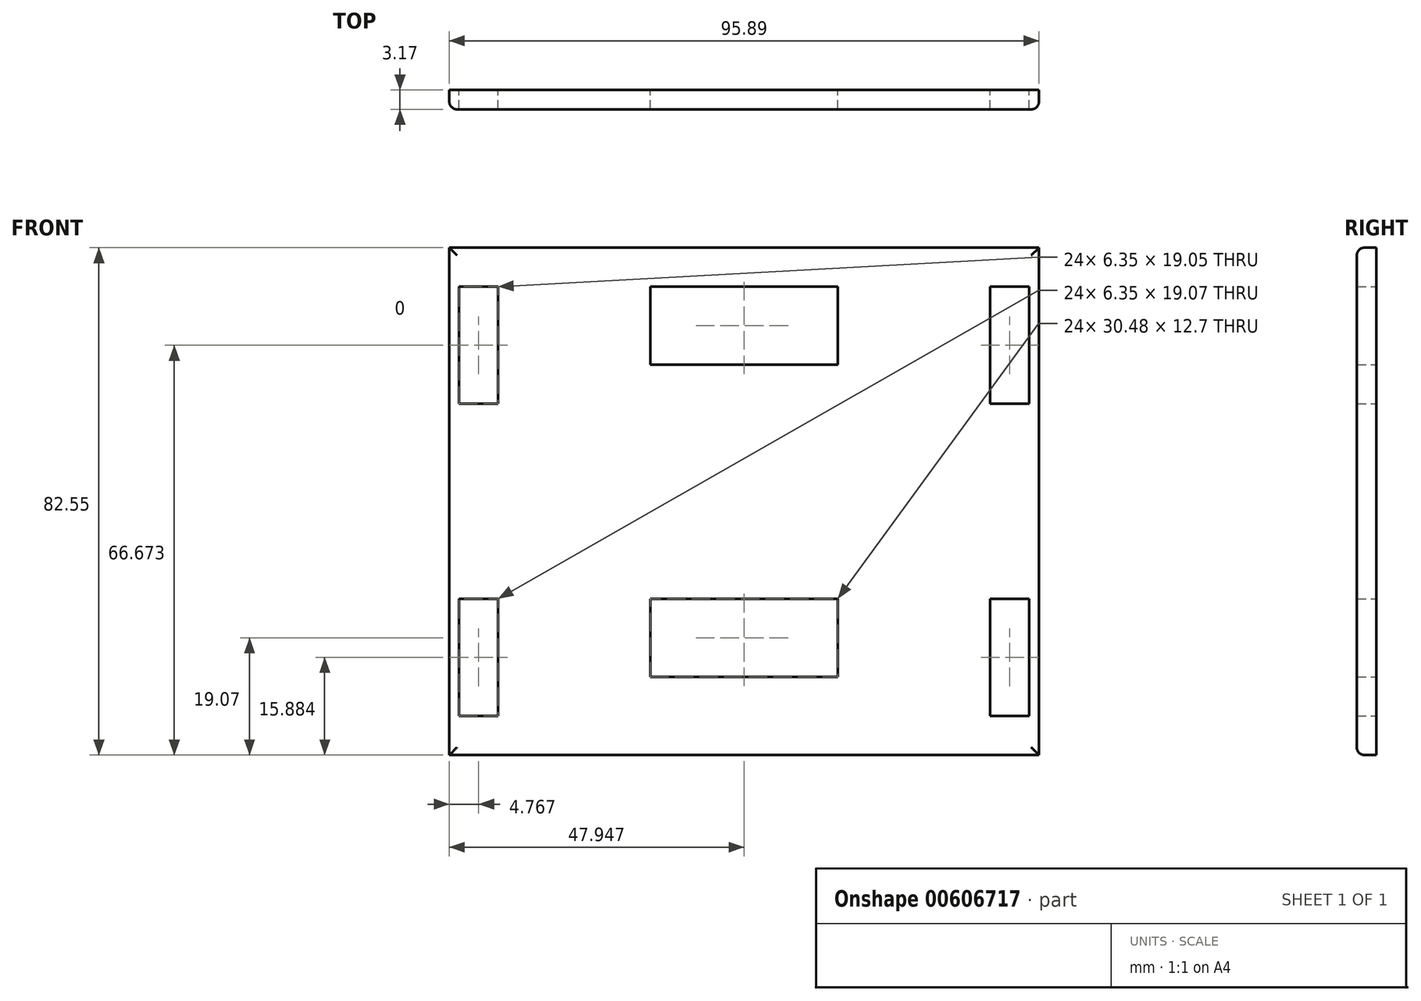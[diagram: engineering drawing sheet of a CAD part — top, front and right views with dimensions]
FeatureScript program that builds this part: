
annotation { "Feature Type Name" : "Feature", "Feature Type Description" : "" }
export const myFeature = defineFeature(function(context is Context, id is Id, definition is map)
    precondition{}
    {
        {
            var Q0;
            Q0=qCreatedBy(makeId("Front.planeOp"),FACE);
            var sketch = newSketch(context, id + "F0", { "sketchPlane" : qUnion([Q0])});
            skLineSegment(sketch, "E0", {"start": v(-18.63, 68.66) * mm, "end": v(-18.63, -13.9) * mm});
            skLineSegment(sketch, "E1", {"start": v(-13.86, 62.3) * mm, "end": v(-10.69, 62.3) * mm});
            skLineSegment(sketch, "E2", {"start": v(-10.69, 62.3) * mm, "end": v(-10.69, 43.26) * mm});
            skLineSegment(sketch, "E3", {"start": v(-10.69, 43.26) * mm, "end": v(-17.04, 43.26) * mm});
            skLineSegment(sketch, "E4", {"start": v(-17.04, 43.26) * mm, "end": v(-17.04, 62.3) * mm});
            skLineSegment(sketch, "E5", {"start": v(-17.04, 62.3) * mm, "end": v(-13.86, 62.3) * mm});
            skLineSegment(sketch, "E6", {"start": v(-17.04, 11.53) * mm, "end": v(-10.69, 11.53) * mm});
            skLineSegment(sketch, "E7", {"start": v(-10.69, 11.53) * mm, "end": v(-10.69, -7.54) * mm});
            skLineSegment(sketch, "E8", {"start": v(-10.69, -7.54) * mm, "end": v(-17.04, -7.52) * mm});
            skLineSegment(sketch, "E9", {"start": v(-17.04, -7.52) * mm, "end": v(-17.04, 11.53) * mm});
            skLineSegment(sketch, "E10.MirrorCS", {"start": v(69.32, 62.3) * mm, "end": v(69.32, 43.26) * mm});
            skLineSegment(sketch, "E11.MirrorCS", {"start": v(72.5, 62.3) * mm, "end": v(69.32, 62.3) * mm});
            skLineSegment(sketch, "E12.MirrorCS", {"start": v(75.67, 62.3) * mm, "end": v(72.5, 62.3) * mm});
            skLineSegment(sketch, "E13.MirrorCS", {"start": v(75.67, 43.26) * mm, "end": v(75.67, 62.3) * mm});
            skLineSegment(sketch, "E14.MirrorCS", {"start": v(69.32, 43.26) * mm, "end": v(75.67, 43.26) * mm});
            skLineSegment(sketch, "E15.MirrorCS", {"start": v(75.67, 11.53) * mm, "end": v(69.32, 11.53) * mm});
            skLineSegment(sketch, "E16.MirrorCS", {"start": v(69.32, 11.53) * mm, "end": v(69.32, -7.54) * mm});
            skLineSegment(sketch, "E17.MirrorCS", {"start": v(75.67, -7.52) * mm, "end": v(75.67, 11.53) * mm});
            skLineSegment(sketch, "E18.MirrorCS", {"start": v(69.32, -7.54) * mm, "end": v(75.67, -7.52) * mm});
            skLineSegment(sketch, "E19.MirrorCS", {"start": v(77.26, 68.66) * mm, "end": v(77.26, -13.9) * mm});
            skLineSegment(sketch, "E20", {"start": v(-18.63, 68.66) * mm, "end": v(77.26, 68.66) * mm});
            skLineSegment(sketch, "E21", {"start": v(29.32, 62.3) * mm, "end": v(44.56, 62.3) * mm});
            skLineSegment(sketch, "E22", {"start": v(44.56, 62.3) * mm, "end": v(44.56, 49.6) * mm});
            skLineSegment(sketch, "E23", {"start": v(44.56, 49.6) * mm, "end": v(14.08, 49.6) * mm});
            skLineSegment(sketch, "E24", {"start": v(14.08, 49.6) * mm, "end": v(14.08, 62.3) * mm});
            skLineSegment(sketch, "E25", {"start": v(14.08, 62.3) * mm, "end": v(29.32, 62.3) * mm});
            skLineSegment(sketch, "E26", {"start": v(29.32, 11.53) * mm, "end": v(44.56, 11.53) * mm});
            skLineSegment(sketch, "E27", {"start": v(44.56, 11.53) * mm, "end": v(44.56, -1.17) * mm});
            skLineSegment(sketch, "E28", {"start": v(44.56, -1.17) * mm, "end": v(14.08, -1.17) * mm});
            skLineSegment(sketch, "E29", {"start": v(14.08, -1.17) * mm, "end": v(14.08, 11.53) * mm});
            skLineSegment(sketch, "E30", {"start": v(14.08, 11.53) * mm, "end": v(29.32, 11.53) * mm});
            skLineSegment(sketch, "E31", {"start": v(-10.69, -7.54) * mm, "end": v(-10.69, -13.9) * mm});
            skLineSegment(sketch, "E32", {"start": v(-18.63, -13.9) * mm, "end": v(77.26, -13.9) * mm});
            skSolve(sketch);
        }
        {
            var Q0;
            Q0=makeQuery(id+"F0.imprint","IMPRINT",FACE,{"disambiguationData":[TD([[makeQuery(id+"F0.imprint","IMPRINT",EDGE,{"derivedFrom":sQuery(id+"F0.wireOp",EDGE,"E0")}),1.0]])]});
            extrude(context, id + "F1", {"entities" : qUnion([Q0]), "depth" : 3.17 * mm, "offsetDistance" : 25.4 * mm});
        }
        {
            var Q0;
            Q0=makeQuery(id+"F1.opExtrude","CAP_EDGE",EDGE,{"disambiguationData":[OSD([sQuery(id+"F0.wireOp",EDGE,"E19.MirrorCS")])],"isStart":false});
            var Q1;
            Q1=makeQuery(id+"F1.opExtrude","CAP_EDGE",EDGE,{"disambiguationData":[OSD([sQuery(id+"F0.wireOp",EDGE,"E20")])],"isStart":false});
            var Q2;
            Q2=makeQuery(id+"F1.opExtrude","CAP_EDGE",EDGE,{"disambiguationData":[OSD([sQuery(id+"F0.wireOp",EDGE,"E0")])],"isStart":false});
            var Q3;
            Q3=makeQuery(id+"F1.opExtrude","CAP_EDGE",EDGE,{"disambiguationData":[OSD([sQuery(id+"F0.wireOp",EDGE,"E32")])],"isStart":false});
            fillet(context, id + "F2", {"entities" : qUnion([Q0, Q1, Q2, Q3]), "radius" : 1.27 * mm, "tangentPropagation" : true, "allowEdgeOverflow" : false});
        }
    });
